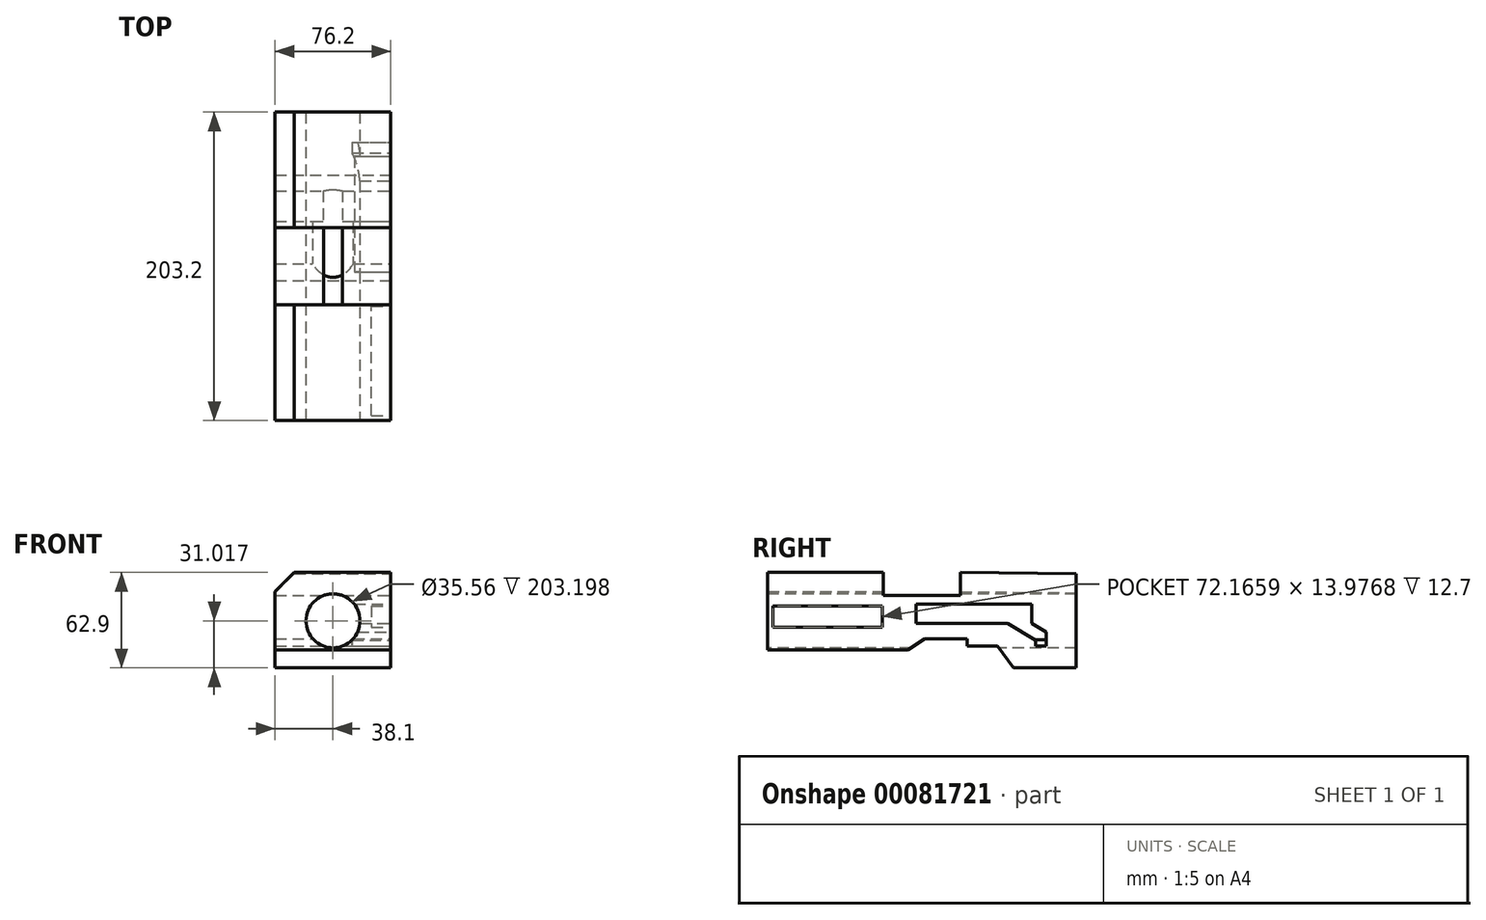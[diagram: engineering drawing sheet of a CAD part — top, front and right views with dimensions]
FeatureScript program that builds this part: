
annotation { "Feature Type Name" : "Feature", "Feature Type Description" : "" }
export const myFeature = defineFeature(function(context is Context, id is Id, definition is map)
    precondition{}
    {
        {
            var Q0;
            Q0=qCreatedBy(makeId("Right.planeOp"),FACE);
            var sketch = newSketch(context, id + "F0", { "sketchPlane" : qUnion([Q0])});
            skLineSegment(sketch, "E0", {"start": v(-131.17, 68.62) * mm, "end": v(-131.17, -34.1) * mm});
            skLineSegment(sketch, "E1", {"start": v(-131.17, -34.1) * mm, "end": v(72.03, -34.1) * mm});
            skLineSegment(sketch, "E2", {"start": v(72.03, -34.1) * mm, "end": v(72.03, 67.5) * mm});
            skLineSegment(sketch, "E3", {"start": v(72.03, 67.5) * mm, "end": v(-131.17, 68.62) * mm});
            skSolve(sketch);
        }
        {
            var Q0;
            Q0 = qSketchRegion(id + "F0", true);
            extrude(context, id + "F1", {"entities" : qUnion([Q0]), "depth" : 76.2 * mm});
        }
        {
            var Q0;
            Q0=makeQuery(id+"F1.opExtrude","CAP_FACE",FACE,{"disambiguationData":[OSD([sQuery(id+"F0.wireOp",EDGE,"E0"),sQuery(id+"F0.wireOp",EDGE,"E1"),sQuery(id+"F0.wireOp",EDGE,"E2"),sQuery(id+"F0.wireOp",EDGE,"E3")])],"isStart":false});
            var sketch = newSketch(context, id + "F2", { "sketchPlane" : qUnion([Q0])});
            skLineSegment(sketch, "E4", {"start": v(-131.17, 62.9) * mm, "end": v(-54.97, 62.9) * mm});
            skLineSegment(sketch, "E5", {"start": v(-54.97, 62.9) * mm, "end": v(-54.97, 47.66) * mm});
            skLineSegment(sketch, "E6", {"start": v(-54.97, 47.66) * mm, "end": v(-4.17, 47.66) * mm});
            skLineSegment(sketch, "E7", {"start": v(-4.17, 47.66) * mm, "end": v(-4.17, 62.9) * mm});
            skLineSegment(sketch, "E8", {"start": v(-4.17, 62.9) * mm, "end": v(72.02, 62.22) * mm});
            skLineSegment(sketch, "E9", {"start": v(-131.17, 62.9) * mm, "end": v(-131.17, 11.84) * mm});
            skLineSegment(sketch, "E10", {"start": v(-131.17, 11.84) * mm, "end": v(-38.9, 11.84) * mm});
            skLineSegment(sketch, "E11", {"start": v(-38.9, 11.84) * mm, "end": v(-27.77, 19.25) * mm});
            skLineSegment(sketch, "E12", {"start": v(-27.77, 19.25) * mm, "end": v(0, 19.25) * mm});
            skLineSegment(sketch, "E13", {"start": v(0, 19.25) * mm, "end": v(0, 14.4) * mm});
            skLineSegment(sketch, "E14", {"start": v(0, 14.4) * mm, "end": v(20.15, 14.4) * mm});
            skLineSegment(sketch, "E15", {"start": v(20.15, 14.4) * mm, "end": v(30.7, 0) * mm});
            skLineSegment(sketch, "E16", {"start": v(30.7, 0) * mm, "end": v(72.03, 0) * mm});
            skLineSegment(sketch, "E17", {"start": v(72.03, 0) * mm, "end": v(72.02, 62.22) * mm});
            skSolve(sketch);
        }
        {
            var Q0;
            {var subQ0=sQuery(id+"F2.wireOp",EDGE,"E10");Q0=makeQuery(id+"F2.imprint","IMPRINT",FACE,{"disambiguationData":[TD([[makeQuery(id+"F2.imprint","IMPRINT",EDGE,{"derivedFrom":subQ0}),-1.0]])]});}
            var Q1;
            {var subQ3=sQuery(id+"F2.wireOp",EDGE,"E4");Q1=makeQuery(id+"F2.imprint","IMPRINT",FACE,{"disambiguationData":[TD([[makeQuery(id+"F2.imprint","IMPRINT",EDGE,{"derivedFrom":subQ3}),1.0]])]});}
            extrude(context, id + "F3", {"entities" : qUnion([Q0, Q1]), "operationType" : NewBodyOperationType.REMOVE, "oppositeDirection" : true, "depth" : 127 * mm});
        }
        {
            var Q0;
            Q0=makeQuery(id+"F3.boolean.opBoolean","COPY",EDGE,{"derivedFrom":makeQuery(id+"F3.opExtrude","CAP_EDGE",EDGE,{"disambiguationData":[OSD([sQuery(id+"F2.wireOp",EDGE,"E4")])],"isStart":true})});
            var Q1;
            Q1=makeQuery(id+"F3.boolean.opBoolean","COPY",EDGE,{"derivedFrom":makeQuery(id+"F3.opExtrude","CAP_EDGE",EDGE,{"disambiguationData":[OSD([sQuery(id+"F2.wireOp",EDGE,"E8")])],"isStart":true})});
            var Q2;
            Q2=makeQuery(id+"F3.boolean.opBoolean","INTERSECT",EDGE,{"derivedFrom":[makeQuery(id+"F1.opExtrude","CAP_FACE",FACE,{"disambiguationData":[OSD([sQuery(id+"F0.wireOp",EDGE,"E0"),sQuery(id+"F0.wireOp",EDGE,"E1"),sQuery(id+"F0.wireOp",EDGE,"E2"),sQuery(id+"F0.wireOp",EDGE,"E3")])],"isStart":true}),makeQuery(id+"F3.opExtrude","SWEPT_FACE",FACE,{"disambiguationData":[OSD([sQuery(id+"F2.wireOp",EDGE,"E4")])]})]});
            var Q3;
            Q3=makeQuery(id+"F3.boolean.opBoolean","INTERSECT",EDGE,{"derivedFrom":[makeQuery(id+"F1.opExtrude","CAP_FACE",FACE,{"disambiguationData":[OSD([sQuery(id+"F0.wireOp",EDGE,"E0"),sQuery(id+"F0.wireOp",EDGE,"E1"),sQuery(id+"F0.wireOp",EDGE,"E2"),sQuery(id+"F0.wireOp",EDGE,"E3")])],"isStart":true}),makeQuery(id+"F3.opExtrude","SWEPT_FACE",FACE,{"disambiguationData":[OSD([sQuery(id+"F2.wireOp",EDGE,"E8")])]})]});
            chamfer(context, id + "F4", {"entities" : qUnion([Q0, Q1, Q2, Q3]), "width" : 12.7 * mm, "tangentPropagation" : true});
        }
        {
            var Q0;
            Q0=makeQuery(id+"F1.opExtrude","SWEPT_FACE",FACE,{"disambiguationData":[OSD([sQuery(id+"F0.wireOp",EDGE,"E0")])]});
            var sketch = newSketch(context, id + "F5", { "sketchPlane" : qUnion([Q0])});
            skCircle(sketch, "E18", {"center": v(38.1, 31.02) * mm, "radius": 12.7 * mm});
            skPoint(sketch, "E18.centerSnap0", {"position": v(76.2, 31.02) * mm});
            skPoint(sketch, "E18.centerSnap1", {"position": v(38.1, 62.9) * mm});
            skCircle(sketch, "E19", {"center": v(38.1, 31.02) * mm, "radius": 17.78 * mm});
            skSolve(sketch);
        }
        {
            var Q0;
            Q0 = qSketchRegion(id + "F5", true);
            var Q1;
            Q1=makeQuery(id+"F5.imprint","IMPRINT",FACE,{"disambiguationData":[TD([[makeQuery(id+"F5.imprint","IMPRINT",EDGE,{"derivedFrom":sQuery(id+"F5.wireOp",EDGE,"E18")}),1.0]])]});
            extrude(context, id + "F6", {"entities" : qUnion([Q0, Q1]), "operationType" : NewBodyOperationType.REMOVE, "oppositeDirection" : true, "depth" : 254 * mm});
        }
        {
            var Q0;
            Q0=makeQuery(id+"F1.opExtrude","CAP_FACE",FACE,{"disambiguationData":[OSD([sQuery(id+"F0.wireOp",EDGE,"E0"),sQuery(id+"F0.wireOp",EDGE,"E1"),sQuery(id+"F0.wireOp",EDGE,"E2"),sQuery(id+"F0.wireOp",EDGE,"E3")])],"isStart":false});
            var sketch = newSketch(context, id + "F7", { "sketchPlane" : qUnion([Q0])});
            skLineSegment(sketch, "E20.bottom", {"start": v(-33.4, 41.95) * mm, "end": v(42.8, 41.95) * mm});
            skLineSegment(sketch, "E20.top", {"start": v(-33.4, 29.25) * mm, "end": v(26.67, 29.25) * mm});
            skLineSegment(sketch, "E20.left", {"start": v(-33.4, 41.95) * mm, "end": v(-33.4, 29.25) * mm});
            skLineSegment(sketch, "E20.right", {"start": v(42.8, 41.95) * mm, "end": v(42.8, 29.25) * mm});
            skLineSegment(sketch, "E21", {"start": v(42.8, 29.25) * mm, "end": v(52.24, 23.58) * mm});
            skLineSegment(sketch, "E22", {"start": v(52.24, 23.58) * mm, "end": v(52.24, 14.49) * mm});
            skLineSegment(sketch, "E23", {"start": v(52.24, 14.49) * mm, "end": v(45.23, 14.49) * mm});
            skLineSegment(sketch, "E24", {"start": v(45.23, 14.49) * mm, "end": v(45.23, 18.09) * mm});
            skLineSegment(sketch, "E25", {"start": v(45.23, 18.09) * mm, "end": v(26.67, 29.25) * mm});
            skSolve(sketch);
        }
        {
            var Q0;
            Q0 = qSketchRegion(id + "F7", true);
            extrude(context, id + "F8", {"entities" : qUnion([Q0]), "operationType" : NewBodyOperationType.REMOVE, "oppositeDirection" : true, "depth" : 25.4 * mm});
        }
        {
            var Q0;
            Q0=makeQuery(id+"F1.opExtrude","CAP_FACE",FACE,{"disambiguationData":[OSD([sQuery(id+"F0.wireOp",EDGE,"E0"),sQuery(id+"F0.wireOp",EDGE,"E1"),sQuery(id+"F0.wireOp",EDGE,"E2"),sQuery(id+"F0.wireOp",EDGE,"E3")])],"isStart":false});
            var sketch = newSketch(context, id + "F9", { "sketchPlane" : qUnion([Q0])});
            skLineSegment(sketch, "E26.bottom", {"start": v(-127.9, 40.93) * mm, "end": v(-55.73, 40.93) * mm});
            skLineSegment(sketch, "E26.top", {"start": v(-127.9, 26.96) * mm, "end": v(-55.73, 26.96) * mm});
            skLineSegment(sketch, "E26.left", {"start": v(-127.9, 40.93) * mm, "end": v(-127.9, 26.96) * mm});
            skLineSegment(sketch, "E26.right", {"start": v(-55.73, 40.93) * mm, "end": v(-55.73, 26.96) * mm});
            skSolve(sketch);
        }
        {
            var Q0;
            Q0=makeQuery(id+"F9.imprint","IMPRINT",FACE,{"disambiguationData":[TD([[makeQuery(id+"F9.imprint","IMPRINT",EDGE,{"derivedFrom":sQuery(id+"F9.wireOp",EDGE,"E26.bottom")}),-1.0]])]});
            extrude(context, id + "F10", {"entities" : qUnion([Q0]), "operationType" : NewBodyOperationType.REMOVE, "oppositeDirection" : true, "depth" : 12.7 * mm});
        }
    });
